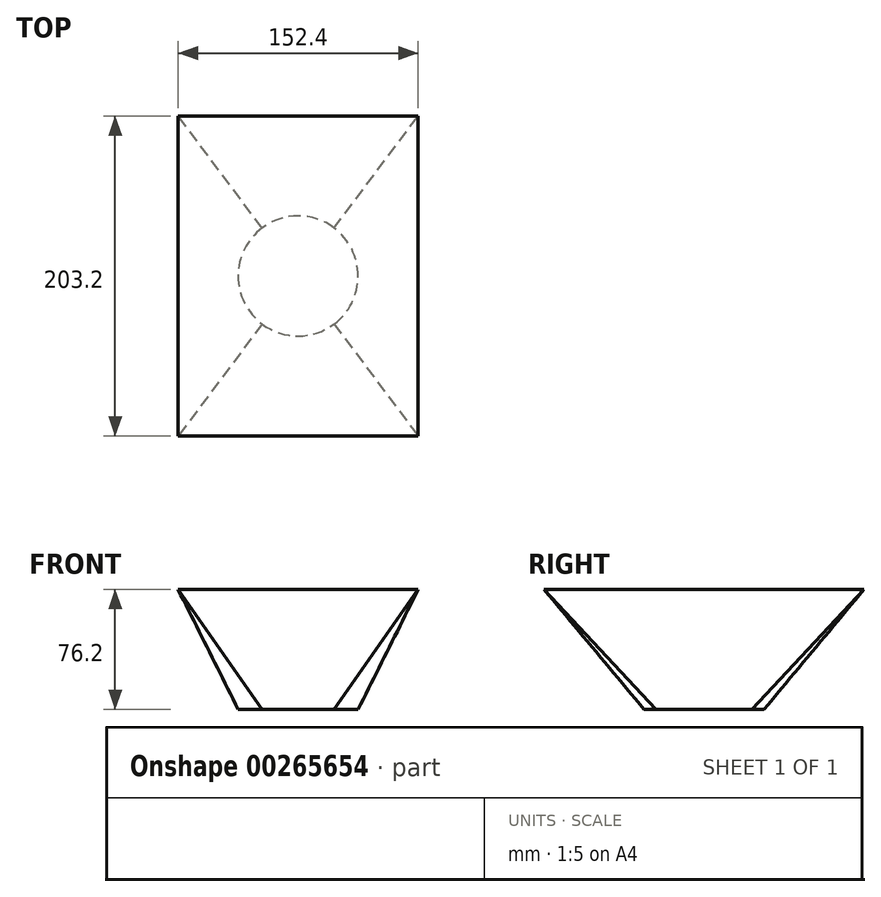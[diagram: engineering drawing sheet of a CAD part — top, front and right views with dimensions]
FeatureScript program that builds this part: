
annotation { "Feature Type Name" : "Feature", "Feature Type Description" : "" }
export const myFeature = defineFeature(function(context is Context, id is Id, definition is map)
    precondition{}
    {
        {
            var Q0;
            Q0=qCreatedBy(makeId("Top.planeOp"),FACE);
            cPlane(context, id + "F0", {"entities" : qUnion([Q0]), "cplaneType" : CPlaneType.OFFSET, "offset" : 76.2 * mm, "width" : 152.4 * mm, "height" : 152.4 * mm});
        }
        {
            var Q0;
            Q0=qCreatedBy(id+"F0.planeOp",FACE);
            var sketch = newSketch(context, id + "F1", { "sketchPlane" : qUnion([Q0])});
            skLineSegment(sketch, "E0.bottom", {"start": v(-76.2, -101.6) * mm, "end": v(76.2, -101.6) * mm});
            skLineSegment(sketch, "E0.top", {"start": v(-76.2, 101.6) * mm, "end": v(76.2, 101.6) * mm});
            skLineSegment(sketch, "E0.left", {"start": v(-76.2, -101.6) * mm, "end": v(-76.2, 101.6) * mm});
            skLineSegment(sketch, "E0.right", {"start": v(76.2, -101.6) * mm, "end": v(76.2, 101.6) * mm});
            skPoint(sketch, "E0.middle", {"position": v(0, 0) * mm});
            skSolve(sketch);
        }
        {
            var Q0;
            Q0=qCreatedBy(makeId("Top.planeOp"),FACE);
            var sketch = newSketch(context, id + "F2", { "sketchPlane" : qUnion([Q0])});
            skLineSegment(sketch, "E1.0", {"start": v(-76.2, 101.6) * mm, "end": v(76.2, 101.6) * mm});
            skLineSegment(sketch, "E1.1", {"start": v(-76.2, -101.6) * mm, "end": v(-76.2, 101.6) * mm});
            skLineSegment(sketch, "E1.2", {"start": v(76.2, -101.6) * mm, "end": v(76.2, 101.6) * mm});
            skLineSegment(sketch, "E1.3", {"start": v(-76.2, -101.6) * mm, "end": v(76.2, -101.6) * mm});
            skLineSegment(sketch, "E2", {"start": v(-76.2, 101.6) * mm, "end": v(76.2, -101.6) * mm, "construction": true});
            skLineSegment(sketch, "E3", {"start": v(76.2, 101.6) * mm, "end": v(22.86, 30.48) * mm, "construction": true});
            skArc(sketch, "E4", {"start": v(-22.86, -30.48) * mm, "mid": v(0, -38.1) * mm, "end": v(22.86, -30.48) * mm});
            skArc(sketch, "E5", {"start": v(22.86, -30.48) * mm, "mid": v(38.1, 0) * mm, "end": v(22.86, 30.48) * mm});
            skLineSegment(sketch, "E6", {"start": v(22.86, 30.48) * mm, "end": v(-76.2, -101.6) * mm, "construction": true});
            skArc(sketch, "E7", {"start": v(-22.86, 30.48) * mm, "mid": v(-38.1, 0) * mm, "end": v(-22.86, -30.48) * mm});
            skArc(sketch, "E8", {"start": v(22.86, 30.48) * mm, "mid": v(0, 38.1) * mm, "end": v(-22.86, 30.48) * mm});
            skSolve(sketch);
        }
        {
            var Q0;
            Q0=makeQuery(id+"F2.imprint","IMPRINT",FACE,{"disambiguationData":[TD([[makeQuery(id+"F2.imprint","IMPRINT",EDGE,{"derivedFrom":sQuery(id+"F2.wireOp",EDGE,"E4")}),1.0]])]});
            var Q1;
            Q1=makeQuery(id+"F1.imprint","IMPRINT",FACE,{"disambiguationData":[TD([[makeQuery(id+"F1.imprint","IMPRINT",EDGE,{"derivedFrom":sQuery(id+"F1.wireOp",EDGE,"E0.bottom")}),1.0]])]});
            loft(context, id + "F3", {"sheetProfilesArray" : [{ "sheetProfileEntities" : qUnion([Q0]) }, { "sheetProfileEntities" : qUnion([Q1]) }]});
        }
    });
